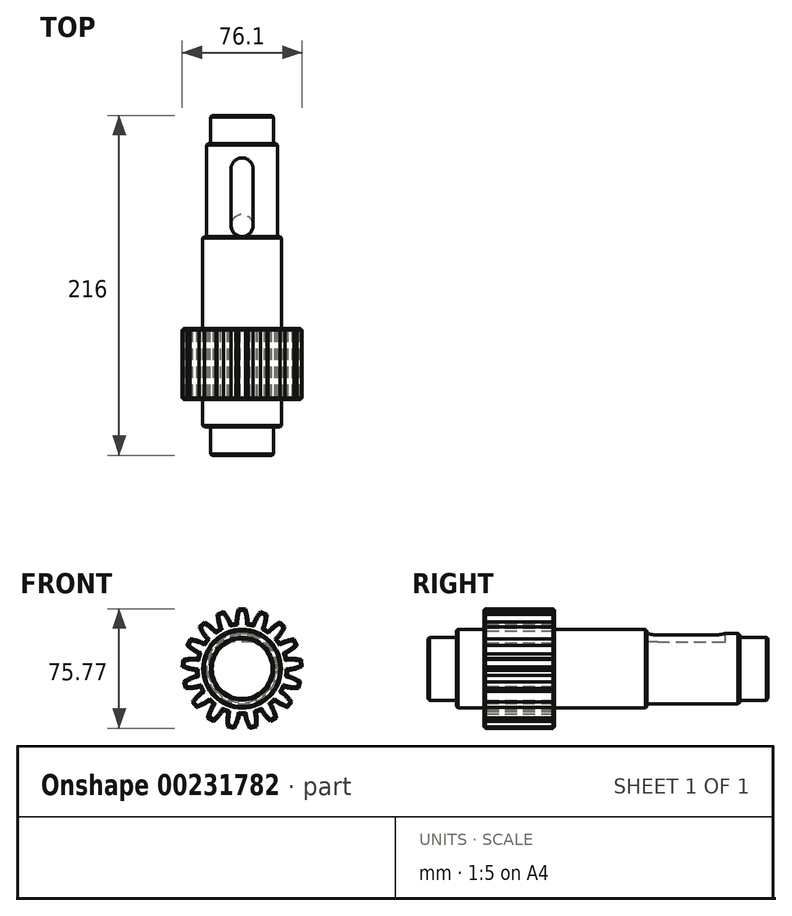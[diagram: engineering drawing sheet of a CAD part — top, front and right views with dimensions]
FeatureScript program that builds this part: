
annotation { "Feature Type Name" : "Feature", "Feature Type Description" : "" }
export const myFeature = defineFeature(function(context is Context, id is Id, definition is map)
    precondition{}
    {
        {
            var Q0;
            Q0=qCreatedBy(makeId("Front.planeOp"),FACE);
            var sketch = newSketch(context, id + "F0", { "sketchPlane" : qUnion([Q0])});
            skCircle(sketch, "E0", {"center": v(0, 0) * mm, "radius": 20 * mm});
            skSolve(sketch);
        }
        {
            var Q0;
            Q0 = qSketchRegion(id + "F0", true);
            extrude(context, id + "F1", {"entities" : qUnion([Q0]), "oppositeDirection" : true, "depth" : 18 * mm});
        }
        {
            var Q0;
            Q0=makeQuery(id+"F1.opExtrude","CAP_FACE",FACE,{"disambiguationData":[OSD([sQuery(id+"F0.wireOp",EDGE,"E0")])],"isStart":false});
            var sketch = newSketch(context, id + "F2", { "sketchPlane" : qUnion([Q0])});
            skCircle(sketch, "E1", {"center": v(0, 0) * mm, "radius": 25 * mm});
            skSolve(sketch);
        }
        {
            var Q0;
            Q0 = qSketchRegion(id + "F2", true);
            extrude(context, id + "F3", {"entities" : qUnion([Q0]), "operationType" : NewBodyOperationType.ADD, "depth" : 17.5 * mm});
        }
        {
            var Q0;
            Q0=makeQuery(id+"F3.opExtrude","CAP_FACE",FACE,{"disambiguationData":[OSD([sQuery(id+"F2.wireOp",EDGE,"E1")])],"isStart":false});
            var sketch = newSketch(context, id + "F4", { "sketchPlane" : qUnion([Q0])});
            skCircle(sketch, "E2", {"center": v(0, 0) * mm, "radius": 38 * mm, "construction": true});
            skCircle(sketch, "E3.0", {"center": v(0, 0) * mm, "radius": 29 * mm});
            skLineSegment(sketch, "E4", {"start": v(0, 38) * mm, "end": v(2.25, 38) * mm});
            skArc(sketch, "E5", {"start": v(3.78, 28.75) * mm, "mid": v(3.42, 33.44) * mm, "end": v(2.25, 38) * mm});
            skLineSegment(sketch, "E6", {"start": v(0, 29) * mm, "end": v(0, 38) * mm, "construction": true});
            skArc(sketch, "E7.MirrorCS", {"start": v(-3.78, 28.75) * mm, "mid": v(-3.42, 33.44) * mm, "end": v(-2.25, 38) * mm});
            skLineSegment(sketch, "E8.MirrorCS", {"start": v(0, 38) * mm, "end": v(-2.25, 38) * mm});
            skLineSegment(sketch, "E9.1.0", {"start": v(-13.73, 35.43) * mm, "end": v(-11.63, 36.25) * mm});
            skArc(sketch, "E9.1.1", {"start": v(-13.91, 25.44) * mm, "mid": v(-15.27, 29.95) * mm, "end": v(-15.83, 34.62) * mm});
            skLineSegment(sketch, "E9.1.2", {"start": v(-10.48, 27.04) * mm, "end": v(-13.73, 35.43) * mm, "construction": true});
            skArc(sketch, "E9.1.3", {"start": v(-6.86, 28.18) * mm, "mid": v(-8.9, 32.42) * mm, "end": v(-11.63, 36.25) * mm});
            skLineSegment(sketch, "E9.1.4", {"start": v(-13.73, 35.43) * mm, "end": v(-15.83, 34.62) * mm});
            skLineSegment(sketch, "E9.2.0", {"start": v(-25.6, 28.08) * mm, "end": v(-23.94, 29.6) * mm});
            skArc(sketch, "E9.2.1", {"start": v(-22.17, 18.7) * mm, "mid": v(-25.06, 22.41) * mm, "end": v(-27.26, 26.57) * mm});
            skLineSegment(sketch, "E9.2.2", {"start": v(-19.54, 21.43) * mm, "end": v(-25.6, 28.08) * mm, "construction": true});
            skArc(sketch, "E9.2.3", {"start": v(-16.58, 23.8) * mm, "mid": v(-20, 27.02) * mm, "end": v(-23.94, 29.6) * mm});
            skLineSegment(sketch, "E9.2.4", {"start": v(-25.6, 28.08) * mm, "end": v(-27.26, 26.57) * mm});
            skLineSegment(sketch, "E9.3.0", {"start": v(-34.02, 16.94) * mm, "end": v(-33.01, 18.95) * mm});
            skArc(sketch, "E9.3.1", {"start": v(-27.42, 9.43) * mm, "mid": v(-31.46, 11.85) * mm, "end": v(-35.02, 14.92) * mm});
            skLineSegment(sketch, "E9.3.2", {"start": v(-25.96, 12.93) * mm, "end": v(-34.02, 16.94) * mm, "construction": true});
            skArc(sketch, "E9.3.3", {"start": v(-24.05, 16.2) * mm, "mid": v(-28.41, 17.97) * mm, "end": v(-33.01, 18.95) * mm});
            skLineSegment(sketch, "E9.3.4", {"start": v(-34.02, 16.94) * mm, "end": v(-35.02, 14.92) * mm});
            skLineSegment(sketch, "E9.4.0", {"start": v(-37.84, 3.5) * mm, "end": v(-37.63, 5.75) * mm});
            skArc(sketch, "E9.4.1", {"start": v(-28.98, -1.11) * mm, "mid": v(-33.62, -0.32) * mm, "end": v(-38.05, 1.27) * mm});
            skLineSegment(sketch, "E9.4.2", {"start": v(-28.88, 2.68) * mm, "end": v(-37.84, 3.5) * mm, "construction": true});
            skArc(sketch, "E9.4.3", {"start": v(-28.28, 6.42) * mm, "mid": v(-32.98, 6.49) * mm, "end": v(-37.63, 5.75) * mm});
            skLineSegment(sketch, "E9.4.4", {"start": v(-37.84, 3.5) * mm, "end": v(-38.05, 1.27) * mm});
            skLineSegment(sketch, "E9.5.0", {"start": v(-36.55, -10.4) * mm, "end": v(-37.17, -8.24) * mm});
            skArc(sketch, "E9.5.1", {"start": v(-26.62, -11.5) * mm, "mid": v(-31.23, -12.44) * mm, "end": v(-35.93, -12.56) * mm});
            skLineSegment(sketch, "E9.5.2", {"start": v(-27.9, -7.94) * mm, "end": v(-36.55, -10.4) * mm, "construction": true});
            skArc(sketch, "E9.5.3", {"start": v(-28.69, -4.23) * mm, "mid": v(-33.1, -5.86) * mm, "end": v(-37.17, -8.24) * mm});
            skLineSegment(sketch, "E9.5.4", {"start": v(-36.55, -10.4) * mm, "end": v(-35.93, -12.56) * mm});
            skLineSegment(sketch, "E9.6.0", {"start": v(-30.32, -22.9) * mm, "end": v(-31.68, -21.1) * mm});
            skArc(sketch, "E9.6.1", {"start": v(-20.67, -20.35) * mm, "mid": v(-24.63, -22.88) * mm, "end": v(-28.97, -24.7) * mm});
            skLineSegment(sketch, "E9.6.2", {"start": v(-23.14, -17.48) * mm, "end": v(-30.32, -22.9) * mm, "construction": true});
            skArc(sketch, "E9.6.3", {"start": v(-25.22, -14.3) * mm, "mid": v(-28.75, -17.43) * mm, "end": v(-31.68, -21.1) * mm});
            skLineSegment(sketch, "E9.6.4", {"start": v(-30.32, -22.9) * mm, "end": v(-28.97, -24.7) * mm});
            skLineSegment(sketch, "E9.7.0", {"start": v(-20, -32.3) * mm, "end": v(-21.92, -31.12) * mm});
            skArc(sketch, "E9.7.1", {"start": v(-11.92, -26.44) * mm, "mid": v(-14.7, -30.23) * mm, "end": v(-18.1, -33.5) * mm});
            skLineSegment(sketch, "E9.7.2", {"start": v(-15.27, -24.66) * mm, "end": v(-20, -32.3) * mm, "construction": true});
            skArc(sketch, "E9.7.3", {"start": v(-18.35, -22.45) * mm, "mid": v(-20.51, -26.63) * mm, "end": v(-21.92, -31.12) * mm});
            skLineSegment(sketch, "E9.7.4", {"start": v(-20, -32.3) * mm, "end": v(-18.1, -33.5) * mm});
            skLineSegment(sketch, "E9.8.0", {"start": v(-6.98, -37.35) * mm, "end": v(-9.2, -36.94) * mm});
            skArc(sketch, "E9.8.1", {"start": v(-1.57, -28.96) * mm, "mid": v(-2.79, -33.5) * mm, "end": v(-4.77, -37.77) * mm});
            skLineSegment(sketch, "E9.8.2", {"start": v(-5.33, -28.5) * mm, "end": v(-6.98, -37.35) * mm, "construction": true});
            skArc(sketch, "E9.8.3", {"start": v(-9, -27.57) * mm, "mid": v(-9.5, -32.25) * mm, "end": v(-9.2, -36.94) * mm});
            skLineSegment(sketch, "E9.8.4", {"start": v(-6.98, -37.35) * mm, "end": v(-4.77, -37.77) * mm});
            skLineSegment(sketch, "E9.9.0", {"start": v(6.98, -37.35) * mm, "end": v(4.77, -37.77) * mm});
            skArc(sketch, "E9.9.1", {"start": v(9, -27.57) * mm, "mid": v(9.5, -32.25) * mm, "end": v(9.2, -36.94) * mm});
            skLineSegment(sketch, "E9.9.2", {"start": v(5.33, -28.5) * mm, "end": v(6.98, -37.35) * mm, "construction": true});
            skArc(sketch, "E9.9.3", {"start": v(1.57, -28.96) * mm, "mid": v(2.79, -33.5) * mm, "end": v(4.77, -37.77) * mm});
            skLineSegment(sketch, "E9.9.4", {"start": v(6.98, -37.35) * mm, "end": v(9.2, -36.94) * mm});
            skLineSegment(sketch, "E9.10.0", {"start": v(20, -32.3) * mm, "end": v(18.1, -33.5) * mm});
            skArc(sketch, "E9.10.1", {"start": v(18.35, -22.45) * mm, "mid": v(20.51, -26.63) * mm, "end": v(21.92, -31.12) * mm});
            skLineSegment(sketch, "E9.10.2", {"start": v(15.27, -24.66) * mm, "end": v(20, -32.3) * mm, "construction": true});
            skArc(sketch, "E9.10.3", {"start": v(11.92, -26.44) * mm, "mid": v(14.7, -30.23) * mm, "end": v(18.1, -33.5) * mm});
            skLineSegment(sketch, "E9.10.4", {"start": v(20, -32.3) * mm, "end": v(21.92, -31.12) * mm});
            skLineSegment(sketch, "E9.11.0", {"start": v(30.32, -22.9) * mm, "end": v(28.97, -24.7) * mm});
            skArc(sketch, "E9.11.1", {"start": v(25.22, -14.3) * mm, "mid": v(28.75, -17.43) * mm, "end": v(31.68, -21.1) * mm});
            skLineSegment(sketch, "E9.11.2", {"start": v(23.14, -17.48) * mm, "end": v(30.32, -22.9) * mm, "construction": true});
            skArc(sketch, "E9.11.3", {"start": v(20.67, -20.35) * mm, "mid": v(24.63, -22.88) * mm, "end": v(28.97, -24.7) * mm});
            skLineSegment(sketch, "E9.11.4", {"start": v(30.32, -22.9) * mm, "end": v(31.68, -21.1) * mm});
            skLineSegment(sketch, "E9.12.0", {"start": v(36.55, -10.4) * mm, "end": v(35.93, -12.56) * mm});
            skArc(sketch, "E9.12.1", {"start": v(28.69, -4.23) * mm, "mid": v(33.1, -5.86) * mm, "end": v(37.17, -8.24) * mm});
            skLineSegment(sketch, "E9.12.2", {"start": v(27.9, -7.94) * mm, "end": v(36.55, -10.4) * mm, "construction": true});
            skArc(sketch, "E9.12.3", {"start": v(26.62, -11.5) * mm, "mid": v(31.23, -12.44) * mm, "end": v(35.93, -12.56) * mm});
            skLineSegment(sketch, "E9.12.4", {"start": v(36.55, -10.4) * mm, "end": v(37.17, -8.24) * mm});
            skLineSegment(sketch, "E9.13.0", {"start": v(37.84, 3.5) * mm, "end": v(38.05, 1.27) * mm});
            skArc(sketch, "E9.13.1", {"start": v(28.28, 6.42) * mm, "mid": v(32.98, 6.49) * mm, "end": v(37.63, 5.75) * mm});
            skLineSegment(sketch, "E9.13.2", {"start": v(28.88, 2.68) * mm, "end": v(37.84, 3.5) * mm, "construction": true});
            skArc(sketch, "E9.13.3", {"start": v(28.98, -1.11) * mm, "mid": v(33.62, -0.32) * mm, "end": v(38.05, 1.27) * mm});
            skLineSegment(sketch, "E9.13.4", {"start": v(37.84, 3.5) * mm, "end": v(37.63, 5.75) * mm});
            skLineSegment(sketch, "E9.14.0", {"start": v(34.02, 16.94) * mm, "end": v(35.02, 14.92) * mm});
            skArc(sketch, "E9.14.1", {"start": v(24.05, 16.2) * mm, "mid": v(28.41, 17.97) * mm, "end": v(33.01, 18.95) * mm});
            skLineSegment(sketch, "E9.14.2", {"start": v(25.96, 12.93) * mm, "end": v(34.02, 16.94) * mm, "construction": true});
            skArc(sketch, "E9.14.3", {"start": v(27.42, 9.43) * mm, "mid": v(31.46, 11.85) * mm, "end": v(35.02, 14.92) * mm});
            skLineSegment(sketch, "E9.14.4", {"start": v(34.02, 16.94) * mm, "end": v(33.01, 18.95) * mm});
            skLineSegment(sketch, "E9.15.0", {"start": v(25.6, 28.08) * mm, "end": v(27.26, 26.57) * mm});
            skArc(sketch, "E9.15.1", {"start": v(16.58, 23.8) * mm, "mid": v(20, 27.02) * mm, "end": v(23.94, 29.6) * mm});
            skLineSegment(sketch, "E9.15.2", {"start": v(19.54, 21.43) * mm, "end": v(25.6, 28.08) * mm, "construction": true});
            skArc(sketch, "E9.15.3", {"start": v(22.17, 18.7) * mm, "mid": v(25.06, 22.41) * mm, "end": v(27.26, 26.57) * mm});
            skLineSegment(sketch, "E9.15.4", {"start": v(25.6, 28.08) * mm, "end": v(23.94, 29.6) * mm});
            skLineSegment(sketch, "E9.16.0", {"start": v(13.73, 35.43) * mm, "end": v(15.83, 34.62) * mm});
            skArc(sketch, "E9.16.1", {"start": v(6.86, 28.18) * mm, "mid": v(8.9, 32.42) * mm, "end": v(11.63, 36.25) * mm});
            skLineSegment(sketch, "E9.16.2", {"start": v(10.48, 27.04) * mm, "end": v(13.73, 35.43) * mm, "construction": true});
            skArc(sketch, "E9.16.3", {"start": v(13.91, 25.44) * mm, "mid": v(15.27, 29.95) * mm, "end": v(15.83, 34.62) * mm});
            skLineSegment(sketch, "E9.16.4", {"start": v(13.73, 35.43) * mm, "end": v(11.63, 36.25) * mm});
            skSolve(sketch);
        }
        {
            var Q0;
            Q0 = qSketchRegion(id + "F4", true);
            extrude(context, id + "F5", {"entities" : qUnion([Q0]), "operationType" : NewBodyOperationType.ADD, "depth" : 45 * mm});
        }
        {
            var Q0;
            Q0=makeQuery(id+"F5.opExtrude","CAP_FACE",FACE,{"disambiguationData":[OSD([sQuery(id+"F4.wireOp",EDGE,"E3.0"),sQuery(id+"F4.wireOp",EDGE,"E4"),sQuery(id+"F4.wireOp",EDGE,"E5"),sQuery(id+"F4.wireOp",EDGE,"E7.MirrorCS"),sQuery(id+"F4.wireOp",EDGE,"E8.MirrorCS"),sQuery(id+"F4.wireOp",EDGE,"E9.1.0"),sQuery(id+"F4.wireOp",EDGE,"E9.1.1"),sQuery(id+"F4.wireOp",EDGE,"E9.1.3"),sQuery(id+"F4.wireOp",EDGE,"E9.1.4"),sQuery(id+"F4.wireOp",EDGE,"E9.2.0"),sQuery(id+"F4.wireOp",EDGE,"E9.2.1"),sQuery(id+"F4.wireOp",EDGE,"E9.2.3"),sQuery(id+"F4.wireOp",EDGE,"E9.2.4"),sQuery(id+"F4.wireOp",EDGE,"E9.3.0"),sQuery(id+"F4.wireOp",EDGE,"E9.3.1"),sQuery(id+"F4.wireOp",EDGE,"E9.3.3"),sQuery(id+"F4.wireOp",EDGE,"E9.3.4"),sQuery(id+"F4.wireOp",EDGE,"E9.4.0"),sQuery(id+"F4.wireOp",EDGE,"E9.4.1"),sQuery(id+"F4.wireOp",EDGE,"E9.4.3"),sQuery(id+"F4.wireOp",EDGE,"E9.4.4"),sQuery(id+"F4.wireOp",EDGE,"E9.5.0"),sQuery(id+"F4.wireOp",EDGE,"E9.5.1"),sQuery(id+"F4.wireOp",EDGE,"E9.5.3"),sQuery(id+"F4.wireOp",EDGE,"E9.5.4"),sQuery(id+"F4.wireOp",EDGE,"E9.6.0"),sQuery(id+"F4.wireOp",EDGE,"E9.6.1"),sQuery(id+"F4.wireOp",EDGE,"E9.6.3"),sQuery(id+"F4.wireOp",EDGE,"E9.6.4"),sQuery(id+"F4.wireOp",EDGE,"E9.7.0"),sQuery(id+"F4.wireOp",EDGE,"E9.7.1"),sQuery(id+"F4.wireOp",EDGE,"E9.7.3"),sQuery(id+"F4.wireOp",EDGE,"E9.7.4"),sQuery(id+"F4.wireOp",EDGE,"E9.8.0"),sQuery(id+"F4.wireOp",EDGE,"E9.8.1"),sQuery(id+"F4.wireOp",EDGE,"E9.8.3"),sQuery(id+"F4.wireOp",EDGE,"E9.8.4"),sQuery(id+"F4.wireOp",EDGE,"E9.9.0"),sQuery(id+"F4.wireOp",EDGE,"E9.9.1"),sQuery(id+"F4.wireOp",EDGE,"E9.9.3"),sQuery(id+"F4.wireOp",EDGE,"E9.9.4"),sQuery(id+"F4.wireOp",EDGE,"E9.10.0"),sQuery(id+"F4.wireOp",EDGE,"E9.10.1"),sQuery(id+"F4.wireOp",EDGE,"E9.10.3"),sQuery(id+"F4.wireOp",EDGE,"E9.10.4"),sQuery(id+"F4.wireOp",EDGE,"E9.11.0"),sQuery(id+"F4.wireOp",EDGE,"E9.11.1"),sQuery(id+"F4.wireOp",EDGE,"E9.11.3"),sQuery(id+"F4.wireOp",EDGE,"E9.11.4"),sQuery(id+"F4.wireOp",EDGE,"E9.12.0"),sQuery(id+"F4.wireOp",EDGE,"E9.12.1"),sQuery(id+"F4.wireOp",EDGE,"E9.12.3"),sQuery(id+"F4.wireOp",EDGE,"E9.12.4"),sQuery(id+"F4.wireOp",EDGE,"E9.13.0"),sQuery(id+"F4.wireOp",EDGE,"E9.13.1"),sQuery(id+"F4.wireOp",EDGE,"E9.13.3"),sQuery(id+"F4.wireOp",EDGE,"E9.13.4"),sQuery(id+"F4.wireOp",EDGE,"E9.14.0"),sQuery(id+"F4.wireOp",EDGE,"E9.14.1"),sQuery(id+"F4.wireOp",EDGE,"E9.14.3"),sQuery(id+"F4.wireOp",EDGE,"E9.14.4"),sQuery(id+"F4.wireOp",EDGE,"E9.15.0"),sQuery(id+"F4.wireOp",EDGE,"E9.15.1"),sQuery(id+"F4.wireOp",EDGE,"E9.15.3"),sQuery(id+"F4.wireOp",EDGE,"E9.15.4"),sQuery(id+"F4.wireOp",EDGE,"E9.16.0"),sQuery(id+"F4.wireOp",EDGE,"E9.16.1"),sQuery(id+"F4.wireOp",EDGE,"E9.16.3"),sQuery(id+"F4.wireOp",EDGE,"E9.16.4")])],"isStart":false});
            var sketch = newSketch(context, id + "F6", { "sketchPlane" : qUnion([Q0])});
            skCircle(sketch, "E10", {"center": v(0, 0) * mm, "radius": 25 * mm});
            skSolve(sketch);
        }
        {
            var Q0;
            Q0 = qSketchRegion(id + "F6", true);
            extrude(context, id + "F7", {"entities" : qUnion([Q0]), "operationType" : NewBodyOperationType.ADD, "depth" : 58.5 * mm});
        }
        {
            var Q0;
            Q0=makeQuery(id+"F7.opExtrude","CAP_FACE",FACE,{"disambiguationData":[OSD([sQuery(id+"F6.wireOp",EDGE,"E10")])],"isStart":false});
            var sketch = newSketch(context, id + "F8", { "sketchPlane" : qUnion([Q0])});
            skCircle(sketch, "E11", {"center": v(0, 0) * mm, "radius": 22.5 * mm});
            skSolve(sketch);
        }
        {
            var Q0;
            Q0 = qSketchRegion(id + "F8", true);
            extrude(context, id + "F9", {"entities" : qUnion([Q0]), "operationType" : NewBodyOperationType.ADD, "depth" : 59 * mm});
        }
        {
            var Q0;
            Q0=makeQuery(id+"F9.opExtrude","CAP_FACE",FACE,{"disambiguationData":[OSD([sQuery(id+"F8.wireOp",EDGE,"E11")])],"isStart":false});
            var sketch = newSketch(context, id + "F10", { "sketchPlane" : qUnion([Q0])});
            skCircle(sketch, "E12", {"center": v(0, 0) * mm, "radius": 20 * mm});
            skSolve(sketch);
        }
        {
            var Q0;
            Q0 = qSketchRegion(id + "F10", true);
            extrude(context, id + "F11", {"entities" : qUnion([Q0]), "operationType" : NewBodyOperationType.ADD, "depth" : 18 * mm});
        }
        {
            var Q0;
            Q0=qCreatedBy(makeId("Top.planeOp"),FACE);
            cPlane(context, id + "F12", {"entities" : qUnion([Q0]), "cplaneType" : CPlaneType.OFFSET, "offset" : 22.5 * mm, "width" : 150 * mm, "height" : 150 * mm});
        }
        {
            var Q0;
            Q0=qCreatedBy(id+"F12.planeOp",FACE);
            var sketch = newSketch(context, id + "F13", { "sketchPlane" : qUnion([Q0])});
            skLineSegment(sketch, "E13.MirrorCS", {"start": v(-7, 146) * mm, "end": v(-7, 182) * mm});
            skLineSegment(sketch, "E14.MirrorCS", {"start": v(7, 146) * mm, "end": v(7, 182) * mm});
            skLineSegment(sketch, "E15", {"start": v(-10.36, 189) * mm, "end": v(12.14, 189) * mm, "construction": true});
            skArc(sketch, "E16", {"start": v(7, 182) * mm, "mid": v(0, 189) * mm, "end": v(-7, 182) * mm});
            skArc(sketch, "E17", {"start": v(-7, 146) * mm, "mid": v(0, 139) * mm, "end": v(7, 146) * mm});
            skSolve(sketch);
        }
        {
            var Q0;
            Q0 = qSketchRegion(id + "F13", true);
            extrude(context, id + "F14", {"entities" : qUnion([Q0]), "operationType" : NewBodyOperationType.REMOVE, "oppositeDirection" : true, "depth" : 5.5 * mm});
        }
        {
            var Q0;
            Q0=makeQuery(id+"F3.opExtrude","CAP_EDGE",EDGE,{"disambiguationData":[OSD([sQuery(id+"F2.wireOp",EDGE,"E1")])],"isStart":true});
            var Q1;
            Q1=makeQuery(id+"F1.opExtrude","CAP_EDGE",EDGE,{"disambiguationData":[OSD([sQuery(id+"F0.wireOp",EDGE,"E0")])],"isStart":true});
            var Q2;
            Q2=makeQuery(id+"F7.opExtrude","CAP_EDGE",EDGE,{"disambiguationData":[OSD([sQuery(id+"F6.wireOp",EDGE,"E10")])],"isStart":false});
            var Q3;
            Q3=makeQuery(id+"F9.opExtrude","CAP_EDGE",EDGE,{"disambiguationData":[OSD([sQuery(id+"F8.wireOp",EDGE,"E11")])],"isStart":false});
            var Q4;
            Q4=makeQuery(id+"F11.opExtrude","CAP_EDGE",EDGE,{"disambiguationData":[OSD([sQuery(id+"F10.wireOp",EDGE,"E12")])],"isStart":false});
            chamfer(context, id + "F15", {"entities" : qUnion([Q0, Q1, Q2, Q3, Q4]), "width" : 1 * mm, "tangentPropagation" : true});
        }
        {
            var Q0;
            {var subQ0=sQuery(id+"F4.wireOp",EDGE,"E3.0");Q0=makeQuery(id+"F5.opExtrude","CAP_EDGE",EDGE,{"disambiguationData":[OSD([subQ0]),TDD([makeQuery(id+"F4.imprint","IMPRINT",EDGE,{"disambiguationData":[TD([[makeQuery(id+"F4.imprint","INTERSECT",VERTEX,{"derivedFrom":[subQ0,sQuery(id+"F4.wireOp",EDGE,"E9.3.1")]}),-1.0]])],"derivedFrom":subQ0})])],"isStart":true});}
            var Q1;
            Q1=makeQuery(id+"F5.opExtrude","CAP_EDGE",EDGE,{"disambiguationData":[OSD([sQuery(id+"F4.wireOp",EDGE,"E9.5.1")])],"isStart":true});
            var Q2;
            Q2=makeQuery(id+"F5.opExtrude","CAP_EDGE",EDGE,{"disambiguationData":[OSD([sQuery(id+"F4.wireOp",EDGE,"E9.9.3")])],"isStart":true});
            var Q3;
            {var subQ0=sQuery(id+"F4.wireOp",EDGE,"E3.0");Q3=makeQuery(id+"F5.opExtrude","CAP_EDGE",EDGE,{"disambiguationData":[OSD([subQ0]),TDD([makeQuery(id+"F4.imprint","IMPRINT",EDGE,{"disambiguationData":[TD([[makeQuery(id+"F4.imprint","INTERSECT",VERTEX,{"derivedFrom":[subQ0,sQuery(id+"F4.wireOp",EDGE,"E9.15.1")]}),-1.0]])],"derivedFrom":subQ0})])],"isStart":true});}
            var Q4;
            {var subQ0=sQuery(id+"F4.wireOp",EDGE,"E3.0");Q4=makeQuery(id+"F5.opExtrude","CAP_EDGE",EDGE,{"disambiguationData":[OSD([subQ0]),TDD([makeQuery(id+"F4.imprint","IMPRINT",EDGE,{"disambiguationData":[TD([[makeQuery(id+"F4.imprint","INTERSECT",VERTEX,{"derivedFrom":[subQ0,sQuery(id+"F4.wireOp",EDGE,"E5")]}),1.0]])],"derivedFrom":subQ0})])],"isStart":true});}
            var Q5;
            Q5=makeQuery(id+"F5.opExtrude","CAP_EDGE",EDGE,{"disambiguationData":[OSD([sQuery(id+"F4.wireOp",EDGE,"E9.15.0"),sQuery(id+"F4.wireOp",EDGE,"E9.15.4")])],"isStart":true});
            var Q6;
            Q6=makeQuery(id+"F5.opExtrude","CAP_EDGE",EDGE,{"disambiguationData":[OSD([sQuery(id+"F4.wireOp",EDGE,"E9.16.3")])],"isStart":true});
            var Q7;
            Q7=makeQuery(id+"F5.opExtrude","CAP_EDGE",EDGE,{"disambiguationData":[OSD([sQuery(id+"F4.wireOp",EDGE,"E9.2.1")])],"isStart":true});
            var Q8;
            Q8=makeQuery(id+"F5.opExtrude","CAP_EDGE",EDGE,{"disambiguationData":[OSD([sQuery(id+"F4.wireOp",EDGE,"E9.7.0"),sQuery(id+"F4.wireOp",EDGE,"E9.7.4")])],"isStart":true});
            var Q9;
            Q9=makeQuery(id+"F5.opExtrude","CAP_EDGE",EDGE,{"disambiguationData":[OSD([sQuery(id+"F4.wireOp",EDGE,"E9.6.1")])],"isStart":true});
            var Q10;
            Q10=makeQuery(id+"F5.opExtrude","CAP_EDGE",EDGE,{"disambiguationData":[OSD([sQuery(id+"F4.wireOp",EDGE,"E9.11.3")])],"isStart":true});
            var Q11;
            Q11=makeQuery(id+"F5.opExtrude","CAP_EDGE",EDGE,{"disambiguationData":[OSD([sQuery(id+"F4.wireOp",EDGE,"E9.16.1")])],"isStart":true});
            var Q12;
            Q12=makeQuery(id+"F5.opExtrude","CAP_EDGE",EDGE,{"disambiguationData":[OSD([sQuery(id+"F4.wireOp",EDGE,"E9.2.3")])],"isStart":true});
            var Q13;
            Q13=makeQuery(id+"F5.opExtrude","CAP_EDGE",EDGE,{"disambiguationData":[OSD([sQuery(id+"F4.wireOp",EDGE,"E9.5.3")])],"isStart":true});
            var Q14;
            Q14=makeQuery(id+"F5.opExtrude","CAP_EDGE",EDGE,{"disambiguationData":[OSD([sQuery(id+"F4.wireOp",EDGE,"E9.7.3")])],"isStart":true});
            var Q15;
            Q15=makeQuery(id+"F5.opExtrude","CAP_EDGE",EDGE,{"disambiguationData":[OSD([sQuery(id+"F4.wireOp",EDGE,"E9.13.0"),sQuery(id+"F4.wireOp",EDGE,"E9.13.4")])],"isStart":true});
            var Q16;
            {var subQ0=sQuery(id+"F4.wireOp",EDGE,"E3.0");Q16=makeQuery(id+"F5.opExtrude","CAP_EDGE",EDGE,{"disambiguationData":[OSD([subQ0]),TDD([makeQuery(id+"F4.imprint","IMPRINT",EDGE,{"disambiguationData":[TD([[makeQuery(id+"F4.imprint","INTERSECT",VERTEX,{"derivedFrom":[subQ0,sQuery(id+"F4.wireOp",EDGE,"E7.MirrorCS")]}),-1.0]])],"derivedFrom":subQ0})])],"isStart":true});}
            var Q17;
            {var subQ0=sQuery(id+"F4.wireOp",EDGE,"E3.0");Q17=makeQuery(id+"F5.opExtrude","CAP_EDGE",EDGE,{"disambiguationData":[OSD([subQ0]),TDD([makeQuery(id+"F4.imprint","IMPRINT",EDGE,{"disambiguationData":[TD([[makeQuery(id+"F4.imprint","INTERSECT",VERTEX,{"derivedFrom":[subQ0,sQuery(id+"F4.wireOp",EDGE,"E9.1.1")]}),-1.0]])],"derivedFrom":subQ0})])],"isStart":true});}
            var Q18;
            Q18=makeQuery(id+"F5.opExtrude","CAP_EDGE",EDGE,{"disambiguationData":[OSD([sQuery(id+"F4.wireOp",EDGE,"E9.12.1")])],"isStart":true});
            var Q19;
            {var subQ0=sQuery(id+"F4.wireOp",EDGE,"E3.0");Q19=makeQuery(id+"F5.opExtrude","CAP_EDGE",EDGE,{"disambiguationData":[OSD([subQ0]),TDD([makeQuery(id+"F4.imprint","IMPRINT",EDGE,{"disambiguationData":[TD([[makeQuery(id+"F4.imprint","INTERSECT",VERTEX,{"derivedFrom":[subQ0,sQuery(id+"F4.wireOp",EDGE,"E9.2.1")]}),-1.0]])],"derivedFrom":subQ0})])],"isStart":true});}
            var Q20;
            Q20=makeQuery(id+"F5.opExtrude","CAP_EDGE",EDGE,{"disambiguationData":[OSD([sQuery(id+"F4.wireOp",EDGE,"E9.3.1")])],"isStart":true});
            var Q21;
            Q21=makeQuery(id+"F5.opExtrude","CAP_EDGE",EDGE,{"disambiguationData":[OSD([sQuery(id+"F4.wireOp",EDGE,"E7.MirrorCS")])],"isStart":true});
            var Q22;
            Q22=makeQuery(id+"F5.opExtrude","CAP_EDGE",EDGE,{"disambiguationData":[OSD([sQuery(id+"F4.wireOp",EDGE,"E9.6.3")])],"isStart":true});
            var Q23;
            Q23=makeQuery(id+"F5.opExtrude","CAP_EDGE",EDGE,{"disambiguationData":[OSD([sQuery(id+"F4.wireOp",EDGE,"E9.11.0"),sQuery(id+"F4.wireOp",EDGE,"E9.11.4")])],"isStart":true});
            var Q24;
            Q24=makeQuery(id+"F5.opExtrude","CAP_EDGE",EDGE,{"disambiguationData":[OSD([sQuery(id+"F4.wireOp",EDGE,"E9.8.3")])],"isStart":true});
            var Q25;
            Q25=makeQuery(id+"F5.opExtrude","CAP_EDGE",EDGE,{"disambiguationData":[OSD([sQuery(id+"F4.wireOp",EDGE,"E9.12.3")])],"isStart":true});
            var Q26;
            Q26=makeQuery(id+"F5.opExtrude","CAP_EDGE",EDGE,{"disambiguationData":[OSD([sQuery(id+"F4.wireOp",EDGE,"E9.14.0"),sQuery(id+"F4.wireOp",EDGE,"E9.14.4")])],"isStart":true});
            var Q27;
            Q27=makeQuery(id+"F5.opExtrude","CAP_EDGE",EDGE,{"disambiguationData":[OSD([sQuery(id+"F4.wireOp",EDGE,"E9.4.3")])],"isStart":true});
            var Q28;
            Q28=makeQuery(id+"F5.opExtrude","CAP_EDGE",EDGE,{"disambiguationData":[OSD([sQuery(id+"F4.wireOp",EDGE,"E9.12.0"),sQuery(id+"F4.wireOp",EDGE,"E9.12.4")])],"isStart":true});
            var Q29;
            {var subQ0=sQuery(id+"F4.wireOp",EDGE,"E3.0");Q29=makeQuery(id+"F5.opExtrude","CAP_EDGE",EDGE,{"disambiguationData":[OSD([subQ0]),TDD([makeQuery(id+"F4.imprint","IMPRINT",EDGE,{"disambiguationData":[TD([[makeQuery(id+"F4.imprint","INTERSECT",VERTEX,{"derivedFrom":[subQ0,sQuery(id+"F4.wireOp",EDGE,"E9.7.1")]}),-1.0]])],"derivedFrom":subQ0})])],"isStart":true});}
            var Q30;
            Q30=makeQuery(id+"F5.opExtrude","CAP_EDGE",EDGE,{"disambiguationData":[OSD([sQuery(id+"F4.wireOp",EDGE,"E9.4.0"),sQuery(id+"F4.wireOp",EDGE,"E9.4.4")])],"isStart":true});
            var Q31;
            Q31=makeQuery(id+"F5.opExtrude","CAP_EDGE",EDGE,{"disambiguationData":[OSD([sQuery(id+"F4.wireOp",EDGE,"E9.9.0"),sQuery(id+"F4.wireOp",EDGE,"E9.9.4")])],"isStart":true});
            var Q32;
            Q32=makeQuery(id+"F5.opExtrude","CAP_EDGE",EDGE,{"disambiguationData":[OSD([sQuery(id+"F4.wireOp",EDGE,"E9.4.1")])],"isStart":true});
            var Q33;
            Q33=makeQuery(id+"F5.opExtrude","CAP_EDGE",EDGE,{"disambiguationData":[OSD([sQuery(id+"F4.wireOp",EDGE,"E9.1.3")])],"isStart":true});
            var Q34;
            Q34=makeQuery(id+"F5.opExtrude","CAP_EDGE",EDGE,{"disambiguationData":[OSD([sQuery(id+"F4.wireOp",EDGE,"E9.15.1")])],"isStart":true});
            var Q35;
            Q35=makeQuery(id+"F5.opExtrude","CAP_EDGE",EDGE,{"disambiguationData":[OSD([sQuery(id+"F4.wireOp",EDGE,"E9.10.3")])],"isStart":true});
            var Q36;
            Q36=makeQuery(id+"F5.opExtrude","CAP_EDGE",EDGE,{"disambiguationData":[OSD([sQuery(id+"F4.wireOp",EDGE,"E9.16.0"),sQuery(id+"F4.wireOp",EDGE,"E9.16.4")])],"isStart":true});
            var Q37;
            Q37=makeQuery(id+"F5.opExtrude","CAP_EDGE",EDGE,{"disambiguationData":[OSD([sQuery(id+"F4.wireOp",EDGE,"E4"),sQuery(id+"F4.wireOp",EDGE,"E8.MirrorCS")])],"isStart":true});
            var Q38;
            Q38=makeQuery(id+"F5.opExtrude","CAP_EDGE",EDGE,{"disambiguationData":[OSD([sQuery(id+"F4.wireOp",EDGE,"E9.6.0"),sQuery(id+"F4.wireOp",EDGE,"E9.6.4")])],"isStart":true});
            var Q39;
            Q39=makeQuery(id+"F5.opExtrude","CAP_EDGE",EDGE,{"disambiguationData":[OSD([sQuery(id+"F4.wireOp",EDGE,"E9.15.3")])],"isStart":true});
            var Q40;
            {var subQ0=sQuery(id+"F4.wireOp",EDGE,"E3.0");Q40=makeQuery(id+"F5.opExtrude","CAP_EDGE",EDGE,{"disambiguationData":[OSD([subQ0]),TDD([makeQuery(id+"F4.imprint","IMPRINT",EDGE,{"disambiguationData":[TD([[makeQuery(id+"F4.imprint","INTERSECT",VERTEX,{"derivedFrom":[subQ0,sQuery(id+"F4.wireOp",EDGE,"E9.14.1")]}),-1.0]])],"derivedFrom":subQ0})])],"isStart":true});}
            var Q41;
            Q41=makeQuery(id+"F5.opExtrude","CAP_EDGE",EDGE,{"disambiguationData":[OSD([sQuery(id+"F4.wireOp",EDGE,"E9.3.3")])],"isStart":true});
            var Q42;
            Q42=makeQuery(id+"F5.opExtrude","CAP_EDGE",EDGE,{"disambiguationData":[OSD([sQuery(id+"F4.wireOp",EDGE,"E9.14.1")])],"isStart":true});
            var Q43;
            {var subQ0=sQuery(id+"F4.wireOp",EDGE,"E3.0");Q43=makeQuery(id+"F5.opExtrude","CAP_EDGE",EDGE,{"disambiguationData":[OSD([subQ0]),TDD([makeQuery(id+"F4.imprint","IMPRINT",EDGE,{"disambiguationData":[TD([[makeQuery(id+"F4.imprint","INTERSECT",VERTEX,{"derivedFrom":[subQ0,sQuery(id+"F4.wireOp",EDGE,"E9.5.1")]}),-1.0]])],"derivedFrom":subQ0})])],"isStart":true});}
            var Q44;
            Q44=makeQuery(id+"F5.opExtrude","CAP_EDGE",EDGE,{"disambiguationData":[OSD([sQuery(id+"F4.wireOp",EDGE,"E9.8.0"),sQuery(id+"F4.wireOp",EDGE,"E9.8.4")])],"isStart":true});
            var Q45;
            Q45=makeQuery(id+"F5.opExtrude","CAP_EDGE",EDGE,{"disambiguationData":[OSD([sQuery(id+"F4.wireOp",EDGE,"E9.13.3")])],"isStart":true});
            var Q46;
            Q46=makeQuery(id+"F5.opExtrude","CAP_EDGE",EDGE,{"disambiguationData":[OSD([sQuery(id+"F4.wireOp",EDGE,"E9.3.0"),sQuery(id+"F4.wireOp",EDGE,"E9.3.4")])],"isStart":true});
            var Q47;
            Q47=makeQuery(id+"F5.opExtrude","CAP_EDGE",EDGE,{"disambiguationData":[OSD([sQuery(id+"F4.wireOp",EDGE,"E9.11.1")])],"isStart":true});
            var Q48;
            Q48=makeQuery(id+"F5.opExtrude","CAP_EDGE",EDGE,{"disambiguationData":[OSD([sQuery(id+"F4.wireOp",EDGE,"E9.9.1")])],"isStart":true});
            var Q49;
            {var subQ0=sQuery(id+"F4.wireOp",EDGE,"E3.0");Q49=makeQuery(id+"F5.opExtrude","CAP_EDGE",EDGE,{"disambiguationData":[OSD([subQ0]),TDD([makeQuery(id+"F4.imprint","IMPRINT",EDGE,{"disambiguationData":[TD([[makeQuery(id+"F4.imprint","INTERSECT",VERTEX,{"derivedFrom":[subQ0,sQuery(id+"F4.wireOp",EDGE,"E9.9.1")]}),-1.0]])],"derivedFrom":subQ0})])],"isStart":true});}
            var Q50;
            {var subQ0=sQuery(id+"F4.wireOp",EDGE,"E3.0");Q50=makeQuery(id+"F5.opExtrude","CAP_EDGE",EDGE,{"disambiguationData":[OSD([subQ0]),TDD([makeQuery(id+"F4.imprint","IMPRINT",EDGE,{"disambiguationData":[TD([[makeQuery(id+"F4.imprint","INTERSECT",VERTEX,{"derivedFrom":[subQ0,sQuery(id+"F4.wireOp",EDGE,"E9.13.1")]}),-1.0]])],"derivedFrom":subQ0})])],"isStart":true});}
            var Q51;
            Q51=makeQuery(id+"F5.opExtrude","CAP_EDGE",EDGE,{"disambiguationData":[OSD([sQuery(id+"F4.wireOp",EDGE,"E9.2.0"),sQuery(id+"F4.wireOp",EDGE,"E9.2.4")])],"isStart":true});
            var Q52;
            Q52=makeQuery(id+"F5.opExtrude","CAP_EDGE",EDGE,{"disambiguationData":[OSD([sQuery(id+"F4.wireOp",EDGE,"E9.10.1")])],"isStart":true});
            var Q53;
            Q53=makeQuery(id+"F5.opExtrude","CAP_EDGE",EDGE,{"disambiguationData":[OSD([sQuery(id+"F4.wireOp",EDGE,"E9.14.3")])],"isStart":true});
            var Q54;
            Q54=makeQuery(id+"F5.opExtrude","CAP_EDGE",EDGE,{"disambiguationData":[OSD([sQuery(id+"F4.wireOp",EDGE,"E9.7.1")])],"isStart":true});
            var Q55;
            Q55=makeQuery(id+"F5.opExtrude","CAP_EDGE",EDGE,{"disambiguationData":[OSD([sQuery(id+"F4.wireOp",EDGE,"E9.8.1")])],"isStart":true});
            var Q56;
            Q56=makeQuery(id+"F5.opExtrude","CAP_EDGE",EDGE,{"disambiguationData":[OSD([sQuery(id+"F4.wireOp",EDGE,"E9.1.0"),sQuery(id+"F4.wireOp",EDGE,"E9.1.4")])],"isStart":true});
            var Q57;
            Q57=makeQuery(id+"F5.opExtrude","CAP_EDGE",EDGE,{"disambiguationData":[OSD([sQuery(id+"F4.wireOp",EDGE,"E9.10.0"),sQuery(id+"F4.wireOp",EDGE,"E9.10.4")])],"isStart":true});
            var Q58;
            Q58=makeQuery(id+"F5.opExtrude","CAP_EDGE",EDGE,{"disambiguationData":[OSD([sQuery(id+"F4.wireOp",EDGE,"E9.1.1")])],"isStart":true});
            var Q59;
            {var subQ0=sQuery(id+"F4.wireOp",EDGE,"E3.0");Q59=makeQuery(id+"F5.opExtrude","CAP_EDGE",EDGE,{"disambiguationData":[OSD([subQ0]),TDD([makeQuery(id+"F4.imprint","IMPRINT",EDGE,{"disambiguationData":[TD([[makeQuery(id+"F4.imprint","INTERSECT",VERTEX,{"derivedFrom":[subQ0,sQuery(id+"F4.wireOp",EDGE,"E9.8.1")]}),-1.0]])],"derivedFrom":subQ0})])],"isStart":true});}
            var Q60;
            {var subQ0=sQuery(id+"F4.wireOp",EDGE,"E3.0");Q60=makeQuery(id+"F5.opExtrude","CAP_EDGE",EDGE,{"disambiguationData":[OSD([subQ0]),TDD([makeQuery(id+"F4.imprint","IMPRINT",EDGE,{"disambiguationData":[TD([[makeQuery(id+"F4.imprint","INTERSECT",VERTEX,{"derivedFrom":[subQ0,sQuery(id+"F4.wireOp",EDGE,"E9.12.1")]}),-1.0]])],"derivedFrom":subQ0})])],"isStart":true});}
            var Q61;
            Q61=makeQuery(id+"F5.opExtrude","CAP_EDGE",EDGE,{"disambiguationData":[OSD([sQuery(id+"F4.wireOp",EDGE,"E9.13.1")])],"isStart":true});
            var Q62;
            {var subQ0=sQuery(id+"F4.wireOp",EDGE,"E3.0");Q62=makeQuery(id+"F5.opExtrude","CAP_EDGE",EDGE,{"disambiguationData":[OSD([subQ0]),TDD([makeQuery(id+"F4.imprint","IMPRINT",EDGE,{"disambiguationData":[TD([[makeQuery(id+"F4.imprint","INTERSECT",VERTEX,{"derivedFrom":[subQ0,sQuery(id+"F4.wireOp",EDGE,"E9.4.1")]}),-1.0]])],"derivedFrom":subQ0})])],"isStart":true});}
            var Q63;
            {var subQ0=sQuery(id+"F4.wireOp",EDGE,"E3.0");Q63=makeQuery(id+"F5.opExtrude","CAP_EDGE",EDGE,{"disambiguationData":[OSD([subQ0]),TDD([makeQuery(id+"F4.imprint","IMPRINT",EDGE,{"disambiguationData":[TD([[makeQuery(id+"F4.imprint","INTERSECT",VERTEX,{"derivedFrom":[subQ0,sQuery(id+"F4.wireOp",EDGE,"E9.11.1")]}),-1.0]])],"derivedFrom":subQ0})])],"isStart":true});}
            var Q64;
            Q64=makeQuery(id+"F5.opExtrude","CAP_EDGE",EDGE,{"disambiguationData":[OSD([sQuery(id+"F4.wireOp",EDGE,"E9.5.0"),sQuery(id+"F4.wireOp",EDGE,"E9.5.4")])],"isStart":true});
            var Q65;
            {var subQ0=sQuery(id+"F4.wireOp",EDGE,"E3.0");Q65=makeQuery(id+"F5.opExtrude","CAP_EDGE",EDGE,{"disambiguationData":[OSD([subQ0]),TDD([makeQuery(id+"F4.imprint","IMPRINT",EDGE,{"disambiguationData":[TD([[makeQuery(id+"F4.imprint","INTERSECT",VERTEX,{"derivedFrom":[subQ0,sQuery(id+"F4.wireOp",EDGE,"E9.10.1")]}),-1.0]])],"derivedFrom":subQ0})])],"isStart":true});}
            var Q66;
            Q66=makeQuery(id+"F5.opExtrude","CAP_EDGE",EDGE,{"disambiguationData":[OSD([sQuery(id+"F4.wireOp",EDGE,"E5")])],"isStart":true});
            var Q67;
            {var subQ0=sQuery(id+"F4.wireOp",EDGE,"E3.0");Q67=makeQuery(id+"F5.opExtrude","CAP_EDGE",EDGE,{"disambiguationData":[OSD([subQ0]),TDD([makeQuery(id+"F4.imprint","IMPRINT",EDGE,{"disambiguationData":[TD([[makeQuery(id+"F4.imprint","INTERSECT",VERTEX,{"derivedFrom":[subQ0,sQuery(id+"F4.wireOp",EDGE,"E9.6.1")]}),-1.0]])],"derivedFrom":subQ0})])],"isStart":true});}
            chamfer(context, id + "F16", {"entities" : qUnion([Q0, Q1, Q2, Q3, Q4, Q5, Q6, Q7, Q8, Q9, Q10, Q11, Q12, Q13, Q14, Q15, Q16, Q17, Q18, Q19, Q20, Q21, Q22, Q23, Q24, Q25, Q26, Q27, Q28, Q29, Q30, Q31, Q32, Q33, Q34, Q35, Q36, Q37, Q38, Q39, Q40, Q41, Q42, Q43, Q44, Q45, Q46, Q47, Q48, Q49, Q50, Q51, Q52, Q53, Q54, Q55, Q56, Q57, Q58, Q59, Q60, Q61, Q62, Q63, Q64, Q65, Q66, Q67]), "width" : 1 * mm, "tangentPropagation" : true});
        }
        {
            var Q0;
            Q0=makeQuery(id+"F5.opExtrude","CAP_EDGE",EDGE,{"disambiguationData":[OSD([sQuery(id+"F4.wireOp",EDGE,"E9.4.1")])],"isStart":false});
            var Q1;
            Q1=makeQuery(id+"F5.opExtrude","CAP_EDGE",EDGE,{"disambiguationData":[OSD([sQuery(id+"F4.wireOp",EDGE,"E4"),sQuery(id+"F4.wireOp",EDGE,"E8.MirrorCS")])],"isStart":false});
            var Q2;
            {var subQ0=sQuery(id+"F4.wireOp",EDGE,"E3.0");Q2=makeQuery(id+"F5.opExtrude","CAP_EDGE",EDGE,{"disambiguationData":[OSD([subQ0]),TDD([makeQuery(id+"F4.imprint","IMPRINT",EDGE,{"disambiguationData":[TD([[makeQuery(id+"F4.imprint","INTERSECT",VERTEX,{"derivedFrom":[subQ0,sQuery(id+"F4.wireOp",EDGE,"E9.14.1")]}),-1.0]])],"derivedFrom":subQ0})])],"isStart":false});}
            var Q3;
            Q3=makeQuery(id+"F5.opExtrude","CAP_EDGE",EDGE,{"disambiguationData":[OSD([sQuery(id+"F4.wireOp",EDGE,"E9.15.0"),sQuery(id+"F4.wireOp",EDGE,"E9.15.4")])],"isStart":false});
            var Q4;
            Q4=makeQuery(id+"F5.opExtrude","CAP_EDGE",EDGE,{"disambiguationData":[OSD([sQuery(id+"F4.wireOp",EDGE,"E9.9.0"),sQuery(id+"F4.wireOp",EDGE,"E9.9.4")])],"isStart":false});
            var Q5;
            Q5=makeQuery(id+"F5.opExtrude","CAP_EDGE",EDGE,{"disambiguationData":[OSD([sQuery(id+"F4.wireOp",EDGE,"E9.1.3")])],"isStart":false});
            var Q6;
            Q6=makeQuery(id+"F5.opExtrude","CAP_EDGE",EDGE,{"disambiguationData":[OSD([sQuery(id+"F4.wireOp",EDGE,"E9.6.3")])],"isStart":false});
            var Q7;
            {var subQ0=sQuery(id+"F4.wireOp",EDGE,"E3.0");Q7=makeQuery(id+"F5.opExtrude","CAP_EDGE",EDGE,{"disambiguationData":[OSD([subQ0]),TDD([makeQuery(id+"F4.imprint","IMPRINT",EDGE,{"disambiguationData":[TD([[makeQuery(id+"F4.imprint","INTERSECT",VERTEX,{"derivedFrom":[subQ0,sQuery(id+"F4.wireOp",EDGE,"E9.3.1")]}),-1.0]])],"derivedFrom":subQ0})])],"isStart":false});}
            var Q8;
            Q8=makeQuery(id+"F5.opExtrude","CAP_EDGE",EDGE,{"disambiguationData":[OSD([sQuery(id+"F4.wireOp",EDGE,"E9.12.0"),sQuery(id+"F4.wireOp",EDGE,"E9.12.4")])],"isStart":false});
            var Q9;
            {var subQ0=sQuery(id+"F4.wireOp",EDGE,"E3.0");Q9=makeQuery(id+"F5.opExtrude","CAP_EDGE",EDGE,{"disambiguationData":[OSD([subQ0]),TDD([makeQuery(id+"F4.imprint","IMPRINT",EDGE,{"disambiguationData":[TD([[makeQuery(id+"F4.imprint","INTERSECT",VERTEX,{"derivedFrom":[subQ0,sQuery(id+"F4.wireOp",EDGE,"E9.2.1")]}),-1.0]])],"derivedFrom":subQ0})])],"isStart":false});}
            var Q10;
            Q10=makeQuery(id+"F5.opExtrude","CAP_EDGE",EDGE,{"disambiguationData":[OSD([sQuery(id+"F4.wireOp",EDGE,"E9.1.0"),sQuery(id+"F4.wireOp",EDGE,"E9.1.4")])],"isStart":false});
            var Q11;
            Q11=makeQuery(id+"F5.opExtrude","CAP_EDGE",EDGE,{"disambiguationData":[OSD([sQuery(id+"F4.wireOp",EDGE,"E9.13.1")])],"isStart":false});
            var Q12;
            Q12=makeQuery(id+"F5.opExtrude","CAP_EDGE",EDGE,{"disambiguationData":[OSD([sQuery(id+"F4.wireOp",EDGE,"E9.7.3")])],"isStart":false});
            var Q13;
            Q13=makeQuery(id+"F5.opExtrude","CAP_EDGE",EDGE,{"disambiguationData":[OSD([sQuery(id+"F4.wireOp",EDGE,"E9.13.3")])],"isStart":false});
            var Q14;
            Q14=makeQuery(id+"F5.opExtrude","CAP_EDGE",EDGE,{"disambiguationData":[OSD([sQuery(id+"F4.wireOp",EDGE,"E9.10.3")])],"isStart":false});
            var Q15;
            Q15=makeQuery(id+"F5.opExtrude","CAP_EDGE",EDGE,{"disambiguationData":[OSD([sQuery(id+"F4.wireOp",EDGE,"E9.7.1")])],"isStart":false});
            var Q16;
            Q16=makeQuery(id+"F5.opExtrude","CAP_EDGE",EDGE,{"disambiguationData":[OSD([sQuery(id+"F4.wireOp",EDGE,"E9.9.3")])],"isStart":false});
            var Q17;
            Q17=makeQuery(id+"F5.opExtrude","CAP_EDGE",EDGE,{"disambiguationData":[OSD([sQuery(id+"F4.wireOp",EDGE,"E9.12.1")])],"isStart":false});
            var Q18;
            Q18=makeQuery(id+"F5.opExtrude","CAP_EDGE",EDGE,{"disambiguationData":[OSD([sQuery(id+"F4.wireOp",EDGE,"E9.13.0"),sQuery(id+"F4.wireOp",EDGE,"E9.13.4")])],"isStart":false});
            var Q19;
            Q19=makeQuery(id+"F5.opExtrude","CAP_EDGE",EDGE,{"disambiguationData":[OSD([sQuery(id+"F4.wireOp",EDGE,"E9.3.3")])],"isStart":false});
            var Q20;
            Q20=makeQuery(id+"F5.opExtrude","CAP_EDGE",EDGE,{"disambiguationData":[OSD([sQuery(id+"F4.wireOp",EDGE,"E9.6.1")])],"isStart":false});
            var Q21;
            {var subQ0=sQuery(id+"F4.wireOp",EDGE,"E3.0");Q21=makeQuery(id+"F5.opExtrude","CAP_EDGE",EDGE,{"disambiguationData":[OSD([subQ0]),TDD([makeQuery(id+"F4.imprint","IMPRINT",EDGE,{"disambiguationData":[TD([[makeQuery(id+"F4.imprint","INTERSECT",VERTEX,{"derivedFrom":[subQ0,sQuery(id+"F4.wireOp",EDGE,"E9.13.1")]}),-1.0]])],"derivedFrom":subQ0})])],"isStart":false});}
            var Q22;
            Q22=makeQuery(id+"F5.opExtrude","CAP_EDGE",EDGE,{"disambiguationData":[OSD([sQuery(id+"F4.wireOp",EDGE,"E9.4.3")])],"isStart":false});
            var Q23;
            Q23=makeQuery(id+"F5.opExtrude","CAP_EDGE",EDGE,{"disambiguationData":[OSD([sQuery(id+"F4.wireOp",EDGE,"E9.9.1")])],"isStart":false});
            var Q24;
            Q24=makeQuery(id+"F5.opExtrude","CAP_EDGE",EDGE,{"disambiguationData":[OSD([sQuery(id+"F4.wireOp",EDGE,"E9.15.3")])],"isStart":false});
            var Q25;
            {var subQ0=sQuery(id+"F4.wireOp",EDGE,"E3.0");Q25=makeQuery(id+"F5.opExtrude","CAP_EDGE",EDGE,{"disambiguationData":[OSD([subQ0]),TDD([makeQuery(id+"F4.imprint","IMPRINT",EDGE,{"disambiguationData":[TD([[makeQuery(id+"F4.imprint","INTERSECT",VERTEX,{"derivedFrom":[subQ0,sQuery(id+"F4.wireOp",EDGE,"E7.MirrorCS")]}),-1.0]])],"derivedFrom":subQ0})])],"isStart":false});}
            var Q26;
            Q26=makeQuery(id+"F5.opExtrude","CAP_EDGE",EDGE,{"disambiguationData":[OSD([sQuery(id+"F4.wireOp",EDGE,"E9.5.3")])],"isStart":false});
            var Q27;
            {var subQ0=sQuery(id+"F4.wireOp",EDGE,"E3.0");Q27=makeQuery(id+"F5.opExtrude","CAP_EDGE",EDGE,{"disambiguationData":[OSD([subQ0]),TDD([makeQuery(id+"F4.imprint","IMPRINT",EDGE,{"disambiguationData":[TD([[makeQuery(id+"F4.imprint","INTERSECT",VERTEX,{"derivedFrom":[subQ0,sQuery(id+"F4.wireOp",EDGE,"E9.15.1")]}),-1.0]])],"derivedFrom":subQ0})])],"isStart":false});}
            var Q28;
            Q28=makeQuery(id+"F5.opExtrude","CAP_EDGE",EDGE,{"disambiguationData":[OSD([sQuery(id+"F4.wireOp",EDGE,"E9.2.0"),sQuery(id+"F4.wireOp",EDGE,"E9.2.4")])],"isStart":false});
            var Q29;
            {var subQ0=sQuery(id+"F4.wireOp",EDGE,"E3.0");Q29=makeQuery(id+"F5.opExtrude","CAP_EDGE",EDGE,{"disambiguationData":[OSD([subQ0]),TDD([makeQuery(id+"F4.imprint","IMPRINT",EDGE,{"disambiguationData":[TD([[makeQuery(id+"F4.imprint","INTERSECT",VERTEX,{"derivedFrom":[subQ0,sQuery(id+"F4.wireOp",EDGE,"E5")]}),1.0]])],"derivedFrom":subQ0})])],"isStart":false});}
            var Q30;
            {var subQ0=sQuery(id+"F4.wireOp",EDGE,"E3.0");Q30=makeQuery(id+"F5.opExtrude","CAP_EDGE",EDGE,{"disambiguationData":[OSD([subQ0]),TDD([makeQuery(id+"F4.imprint","IMPRINT",EDGE,{"disambiguationData":[TD([[makeQuery(id+"F4.imprint","INTERSECT",VERTEX,{"derivedFrom":[subQ0,sQuery(id+"F4.wireOp",EDGE,"E9.6.1")]}),-1.0]])],"derivedFrom":subQ0})])],"isStart":false});}
            var Q31;
            Q31=makeQuery(id+"F5.opExtrude","CAP_EDGE",EDGE,{"disambiguationData":[OSD([sQuery(id+"F4.wireOp",EDGE,"E9.16.1")])],"isStart":false});
            var Q32;
            Q32=makeQuery(id+"F5.opExtrude","CAP_EDGE",EDGE,{"disambiguationData":[OSD([sQuery(id+"F4.wireOp",EDGE,"E9.8.0"),sQuery(id+"F4.wireOp",EDGE,"E9.8.4")])],"isStart":false});
            var Q33;
            Q33=makeQuery(id+"F5.opExtrude","CAP_EDGE",EDGE,{"disambiguationData":[OSD([sQuery(id+"F4.wireOp",EDGE,"E9.3.0"),sQuery(id+"F4.wireOp",EDGE,"E9.3.4")])],"isStart":false});
            var Q34;
            Q34=makeQuery(id+"F5.opExtrude","CAP_EDGE",EDGE,{"disambiguationData":[OSD([sQuery(id+"F4.wireOp",EDGE,"E9.5.0"),sQuery(id+"F4.wireOp",EDGE,"E9.5.4")])],"isStart":false});
            var Q35;
            Q35=makeQuery(id+"F5.opExtrude","CAP_EDGE",EDGE,{"disambiguationData":[OSD([sQuery(id+"F4.wireOp",EDGE,"E5")])],"isStart":false});
            var Q36;
            Q36=makeQuery(id+"F5.opExtrude","CAP_EDGE",EDGE,{"disambiguationData":[OSD([sQuery(id+"F4.wireOp",EDGE,"E9.8.3")])],"isStart":false});
            var Q37;
            {var subQ0=sQuery(id+"F4.wireOp",EDGE,"E3.0");Q37=makeQuery(id+"F5.opExtrude","CAP_EDGE",EDGE,{"disambiguationData":[OSD([subQ0]),TDD([makeQuery(id+"F4.imprint","IMPRINT",EDGE,{"disambiguationData":[TD([[makeQuery(id+"F4.imprint","INTERSECT",VERTEX,{"derivedFrom":[subQ0,sQuery(id+"F4.wireOp",EDGE,"E9.1.1")]}),-1.0]])],"derivedFrom":subQ0})])],"isStart":false});}
            var Q38;
            {var subQ0=sQuery(id+"F4.wireOp",EDGE,"E3.0");Q38=makeQuery(id+"F5.opExtrude","CAP_EDGE",EDGE,{"disambiguationData":[OSD([subQ0]),TDD([makeQuery(id+"F4.imprint","IMPRINT",EDGE,{"disambiguationData":[TD([[makeQuery(id+"F4.imprint","INTERSECT",VERTEX,{"derivedFrom":[subQ0,sQuery(id+"F4.wireOp",EDGE,"E9.9.1")]}),-1.0]])],"derivedFrom":subQ0})])],"isStart":false});}
            var Q39;
            Q39=makeQuery(id+"F5.opExtrude","CAP_EDGE",EDGE,{"disambiguationData":[OSD([sQuery(id+"F4.wireOp",EDGE,"E9.11.3")])],"isStart":false});
            var Q40;
            {var subQ0=sQuery(id+"F4.wireOp",EDGE,"E3.0");Q40=makeQuery(id+"F5.opExtrude","CAP_EDGE",EDGE,{"disambiguationData":[OSD([subQ0]),TDD([makeQuery(id+"F4.imprint","IMPRINT",EDGE,{"disambiguationData":[TD([[makeQuery(id+"F4.imprint","INTERSECT",VERTEX,{"derivedFrom":[subQ0,sQuery(id+"F4.wireOp",EDGE,"E9.5.1")]}),-1.0]])],"derivedFrom":subQ0})])],"isStart":false});}
            var Q41;
            Q41=makeQuery(id+"F5.opExtrude","CAP_EDGE",EDGE,{"disambiguationData":[OSD([sQuery(id+"F4.wireOp",EDGE,"E7.MirrorCS")])],"isStart":false});
            var Q42;
            Q42=makeQuery(id+"F5.opExtrude","CAP_EDGE",EDGE,{"disambiguationData":[OSD([sQuery(id+"F4.wireOp",EDGE,"E9.10.1")])],"isStart":false});
            var Q43;
            Q43=makeQuery(id+"F5.opExtrude","CAP_EDGE",EDGE,{"disambiguationData":[OSD([sQuery(id+"F4.wireOp",EDGE,"E9.11.1")])],"isStart":false});
            var Q44;
            {var subQ0=sQuery(id+"F4.wireOp",EDGE,"E3.0");Q44=makeQuery(id+"F5.opExtrude","CAP_EDGE",EDGE,{"disambiguationData":[OSD([subQ0]),TDD([makeQuery(id+"F4.imprint","IMPRINT",EDGE,{"disambiguationData":[TD([[makeQuery(id+"F4.imprint","INTERSECT",VERTEX,{"derivedFrom":[subQ0,sQuery(id+"F4.wireOp",EDGE,"E9.11.1")]}),-1.0]])],"derivedFrom":subQ0})])],"isStart":false});}
            var Q45;
            Q45=makeQuery(id+"F5.opExtrude","CAP_EDGE",EDGE,{"disambiguationData":[OSD([sQuery(id+"F4.wireOp",EDGE,"E9.2.3")])],"isStart":false});
            var Q46;
            Q46=makeQuery(id+"F5.opExtrude","CAP_EDGE",EDGE,{"disambiguationData":[OSD([sQuery(id+"F4.wireOp",EDGE,"E9.14.3")])],"isStart":false});
            var Q47;
            {var subQ0=sQuery(id+"F4.wireOp",EDGE,"E3.0");Q47=makeQuery(id+"F5.opExtrude","CAP_EDGE",EDGE,{"disambiguationData":[OSD([subQ0]),TDD([makeQuery(id+"F4.imprint","IMPRINT",EDGE,{"disambiguationData":[TD([[makeQuery(id+"F4.imprint","INTERSECT",VERTEX,{"derivedFrom":[subQ0,sQuery(id+"F4.wireOp",EDGE,"E9.4.1")]}),-1.0]])],"derivedFrom":subQ0})])],"isStart":false});}
            var Q48;
            Q48=makeQuery(id+"F5.opExtrude","CAP_EDGE",EDGE,{"disambiguationData":[OSD([sQuery(id+"F4.wireOp",EDGE,"E9.3.1")])],"isStart":false});
            var Q49;
            {var subQ0=sQuery(id+"F4.wireOp",EDGE,"E3.0");Q49=makeQuery(id+"F5.opExtrude","CAP_EDGE",EDGE,{"disambiguationData":[OSD([subQ0]),TDD([makeQuery(id+"F4.imprint","IMPRINT",EDGE,{"disambiguationData":[TD([[makeQuery(id+"F4.imprint","INTERSECT",VERTEX,{"derivedFrom":[subQ0,sQuery(id+"F4.wireOp",EDGE,"E9.7.1")]}),-1.0]])],"derivedFrom":subQ0})])],"isStart":false});}
            var Q50;
            {var subQ0=sQuery(id+"F4.wireOp",EDGE,"E3.0");Q50=makeQuery(id+"F5.opExtrude","CAP_EDGE",EDGE,{"disambiguationData":[OSD([subQ0]),TDD([makeQuery(id+"F4.imprint","IMPRINT",EDGE,{"disambiguationData":[TD([[makeQuery(id+"F4.imprint","INTERSECT",VERTEX,{"derivedFrom":[subQ0,sQuery(id+"F4.wireOp",EDGE,"E9.12.1")]}),-1.0]])],"derivedFrom":subQ0})])],"isStart":false});}
            var Q51;
            Q51=makeQuery(id+"F5.opExtrude","CAP_EDGE",EDGE,{"disambiguationData":[OSD([sQuery(id+"F4.wireOp",EDGE,"E9.8.1")])],"isStart":false});
            var Q52;
            Q52=makeQuery(id+"F5.opExtrude","CAP_EDGE",EDGE,{"disambiguationData":[OSD([sQuery(id+"F4.wireOp",EDGE,"E9.7.0"),sQuery(id+"F4.wireOp",EDGE,"E9.7.4")])],"isStart":false});
            var Q53;
            Q53=makeQuery(id+"F5.opExtrude","CAP_EDGE",EDGE,{"disambiguationData":[OSD([sQuery(id+"F4.wireOp",EDGE,"E9.5.1")])],"isStart":false});
            var Q54;
            Q54=makeQuery(id+"F5.opExtrude","CAP_EDGE",EDGE,{"disambiguationData":[OSD([sQuery(id+"F4.wireOp",EDGE,"E9.15.1")])],"isStart":false});
            var Q55;
            Q55=makeQuery(id+"F5.opExtrude","CAP_EDGE",EDGE,{"disambiguationData":[OSD([sQuery(id+"F4.wireOp",EDGE,"E9.16.0"),sQuery(id+"F4.wireOp",EDGE,"E9.16.4")])],"isStart":false});
            var Q56;
            Q56=makeQuery(id+"F5.opExtrude","CAP_EDGE",EDGE,{"disambiguationData":[OSD([sQuery(id+"F4.wireOp",EDGE,"E9.14.1")])],"isStart":false});
            var Q57;
            Q57=makeQuery(id+"F5.opExtrude","CAP_EDGE",EDGE,{"disambiguationData":[OSD([sQuery(id+"F4.wireOp",EDGE,"E9.16.3")])],"isStart":false});
            var Q58;
            Q58=makeQuery(id+"F5.opExtrude","CAP_EDGE",EDGE,{"disambiguationData":[OSD([sQuery(id+"F4.wireOp",EDGE,"E9.14.0"),sQuery(id+"F4.wireOp",EDGE,"E9.14.4")])],"isStart":false});
            var Q59;
            {var subQ0=sQuery(id+"F4.wireOp",EDGE,"E3.0");Q59=makeQuery(id+"F5.opExtrude","CAP_EDGE",EDGE,{"disambiguationData":[OSD([subQ0]),TDD([makeQuery(id+"F4.imprint","IMPRINT",EDGE,{"disambiguationData":[TD([[makeQuery(id+"F4.imprint","INTERSECT",VERTEX,{"derivedFrom":[subQ0,sQuery(id+"F4.wireOp",EDGE,"E9.8.1")]}),-1.0]])],"derivedFrom":subQ0})])],"isStart":false});}
            var Q60;
            Q60=makeQuery(id+"F5.opExtrude","CAP_EDGE",EDGE,{"disambiguationData":[OSD([sQuery(id+"F4.wireOp",EDGE,"E9.12.3")])],"isStart":false});
            var Q61;
            Q61=makeQuery(id+"F5.opExtrude","CAP_EDGE",EDGE,{"disambiguationData":[OSD([sQuery(id+"F4.wireOp",EDGE,"E9.2.1")])],"isStart":false});
            var Q62;
            Q62=makeQuery(id+"F5.opExtrude","CAP_EDGE",EDGE,{"disambiguationData":[OSD([sQuery(id+"F4.wireOp",EDGE,"E9.4.0"),sQuery(id+"F4.wireOp",EDGE,"E9.4.4")])],"isStart":false});
            var Q63;
            Q63=makeQuery(id+"F5.opExtrude","CAP_EDGE",EDGE,{"disambiguationData":[OSD([sQuery(id+"F4.wireOp",EDGE,"E9.11.0"),sQuery(id+"F4.wireOp",EDGE,"E9.11.4")])],"isStart":false});
            var Q64;
            Q64=makeQuery(id+"F5.opExtrude","CAP_EDGE",EDGE,{"disambiguationData":[OSD([sQuery(id+"F4.wireOp",EDGE,"E9.10.0"),sQuery(id+"F4.wireOp",EDGE,"E9.10.4")])],"isStart":false});
            var Q65;
            Q65=makeQuery(id+"F5.opExtrude","CAP_EDGE",EDGE,{"disambiguationData":[OSD([sQuery(id+"F4.wireOp",EDGE,"E9.1.1")])],"isStart":false});
            var Q66;
            {var subQ0=sQuery(id+"F4.wireOp",EDGE,"E3.0");Q66=makeQuery(id+"F5.opExtrude","CAP_EDGE",EDGE,{"disambiguationData":[OSD([subQ0]),TDD([makeQuery(id+"F4.imprint","IMPRINT",EDGE,{"disambiguationData":[TD([[makeQuery(id+"F4.imprint","INTERSECT",VERTEX,{"derivedFrom":[subQ0,sQuery(id+"F4.wireOp",EDGE,"E9.10.1")]}),-1.0]])],"derivedFrom":subQ0})])],"isStart":false});}
            var Q67;
            Q67=makeQuery(id+"F5.opExtrude","CAP_EDGE",EDGE,{"disambiguationData":[OSD([sQuery(id+"F4.wireOp",EDGE,"E9.6.0"),sQuery(id+"F4.wireOp",EDGE,"E9.6.4")])],"isStart":false});
            chamfer(context, id + "F17", {"entities" : qUnion([Q0, Q1, Q2, Q3, Q4, Q5, Q6, Q7, Q8, Q9, Q10, Q11, Q12, Q13, Q14, Q15, Q16, Q17, Q18, Q19, Q20, Q21, Q22, Q23, Q24, Q25, Q26, Q27, Q28, Q29, Q30, Q31, Q32, Q33, Q34, Q35, Q36, Q37, Q38, Q39, Q40, Q41, Q42, Q43, Q44, Q45, Q46, Q47, Q48, Q49, Q50, Q51, Q52, Q53, Q54, Q55, Q56, Q57, Q58, Q59, Q60, Q61, Q62, Q63, Q64, Q65, Q66, Q67]), "width" : 1 * mm, "tangentPropagation" : true});
        }
    });
